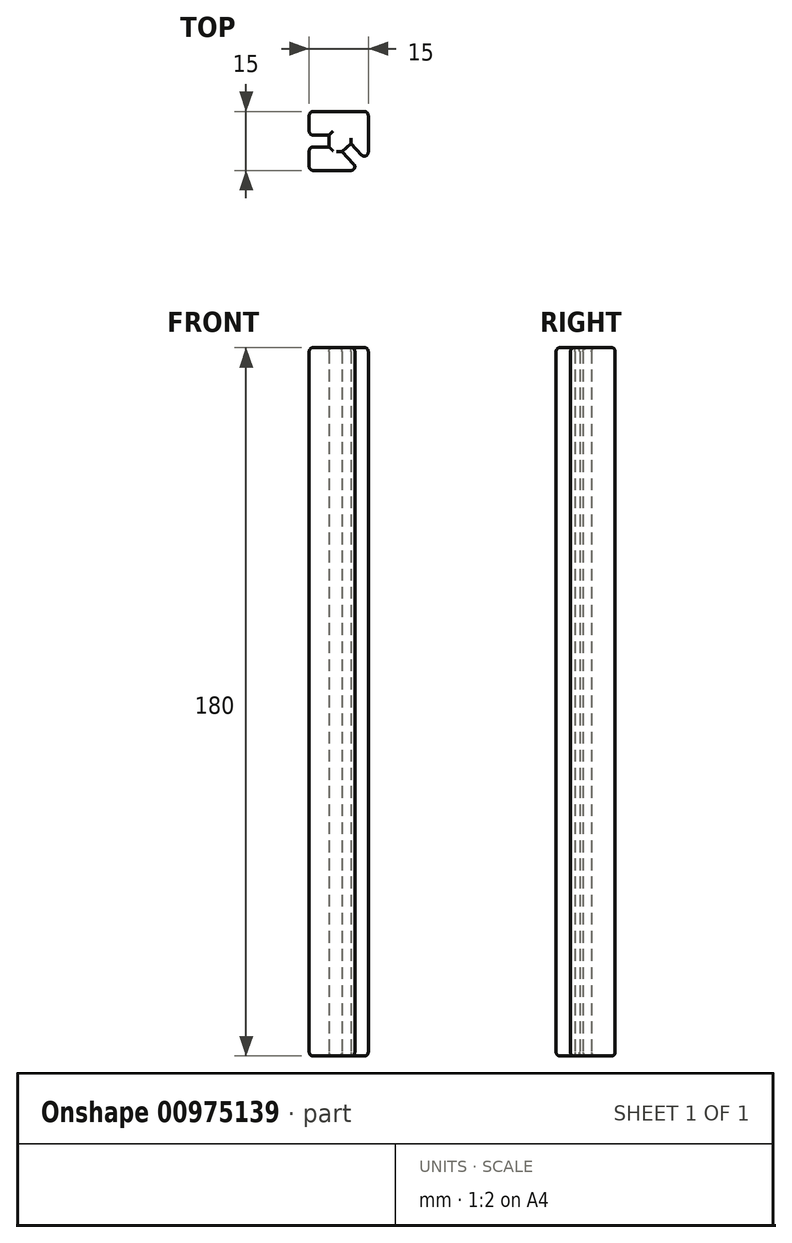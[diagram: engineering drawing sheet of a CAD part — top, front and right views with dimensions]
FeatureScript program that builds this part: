
annotation { "Feature Type Name" : "Feature", "Feature Type Description" : "" }
export const myFeature = defineFeature(function(context is Context, id is Id, definition is map)
    precondition{}
    {
        {
            var Q0;
            Q0=qCreatedBy(makeId("Top.planeOp"),FACE);
            var sketch = newSketch(context, id + "F0", { "sketchPlane" : qUnion([Q0])});
            skLineSegment(sketch, "E0.bottom", {"start": v(-7.5, 7.5) * mm, "end": v(7.5, 7.5) * mm});
            skLineSegment(sketch, "E0.top", {"start": v(-7.5, -7.5) * mm, "end": v(5.43, -7.5) * mm});
            skLineSegment(sketch, "E0.left", {"start": v(-7.5, 7.5) * mm, "end": v(-7.5, 1.5) * mm});
            skLineSegment(sketch, "E0.right", {"start": v(7.5, 7.5) * mm, "end": v(7.5, -5.33) * mm});
            skLineSegment(sketch, "E1.bottom", {"start": v(-7.5, 1.5) * mm, "end": v(-2.5, 1.5) * mm});
            skLineSegment(sketch, "E1.top", {"start": v(-7.5, -1.5) * mm, "end": v(-2.5, -1.5) * mm});
            skLineSegment(sketch, "E1.right", {"start": v(-2.5, 1.5) * mm, "end": v(-2.5, -1.5) * mm});
            skLineSegment(sketch, "E2.trimOffspring", {"start": v(-7.5, -1.5) * mm, "end": v(-7.5, -7.5) * mm});
            skLineSegment(sketch, "E3.0", {"start": v(0.89, -2.75) * mm, "end": v(5.43, -7.5) * mm});
            skLineSegment(sketch, "E4.0", {"start": v(3.06, -0.68) * mm, "end": v(7.5, -5.33) * mm});
            skLineSegment(sketch, "E5", {"start": v(3.06, -0.68) * mm, "end": v(0.89, -2.75) * mm});
            skPoint(sketch, "E6.orphan", {"position": v(7.5, -7.5) * mm});
            skSolve(sketch);
        }
        {
            var Q0;
            Q0=makeQuery(id+"F0.imprint","IMPRINT",FACE,{"disambiguationData":[TD([[makeQuery(id+"F0.imprint","IMPRINT",EDGE,{"derivedFrom":sQuery(id+"F0.wireOp",EDGE,"E0.bottom")}),-1.0]])]});
            extrude(context, id + "F1", {"entities" : qUnion([Q0]), "depth" : 180 * mm, "offsetDistance" : 25 * mm});
        }
        {
            var Q0;
            Q0=makeQuery(id+"F1.opExtrude","CAP_EDGE",EDGE,{"disambiguationData":[OSD([sQuery(id+"F0.wireOp",EDGE,"E1.top")])],"isStart":false});
            var Q1;
            Q1=makeQuery(id+"F1.opExtrude","CAP_EDGE",EDGE,{"disambiguationData":[OSD([sQuery(id+"F0.wireOp",EDGE,"E1.right")])],"isStart":false});
            var Q2;
            Q2=makeQuery(id+"F1.opExtrude","CAP_EDGE",EDGE,{"disambiguationData":[OSD([sQuery(id+"F0.wireOp",EDGE,"E1.bottom")])],"isStart":false});
            var Q3;
            Q3=makeQuery(id+"F1.opExtrude","CAP_EDGE",EDGE,{"disambiguationData":[OSD([sQuery(id+"F0.wireOp",EDGE,"E4.0")])],"isStart":false});
            var Q4;
            Q4=makeQuery(id+"F1.opExtrude","CAP_EDGE",EDGE,{"disambiguationData":[OSD([sQuery(id+"F0.wireOp",EDGE,"E5")])],"isStart":false});
            var Q5;
            Q5=makeQuery(id+"F1.opExtrude","CAP_EDGE",EDGE,{"disambiguationData":[OSD([sQuery(id+"F0.wireOp",EDGE,"E3.0")])],"isStart":false});
            var Q6;
            Q6=makeQuery(id+"F1.opExtrude","CAP_EDGE",EDGE,{"disambiguationData":[OSD([sQuery(id+"F0.wireOp",EDGE,"E0.top")])],"isStart":false});
            var Q7;
            Q7=makeQuery(id+"F1.opExtrude","CAP_EDGE",EDGE,{"disambiguationData":[OSD([sQuery(id+"F0.wireOp",EDGE,"E2.trimOffspring")])],"isStart":false});
            var Q8;
            Q8=makeQuery(id+"F1.opExtrude","CAP_EDGE",EDGE,{"disambiguationData":[OSD([sQuery(id+"F0.wireOp",EDGE,"E0.left")])],"isStart":false});
            var Q9;
            Q9=makeQuery(id+"F1.opExtrude","CAP_EDGE",EDGE,{"disambiguationData":[OSD([sQuery(id+"F0.wireOp",EDGE,"E0.bottom")])],"isStart":false});
            var Q10;
            Q10=makeQuery(id+"F1.opExtrude","CAP_EDGE",EDGE,{"disambiguationData":[OSD([sQuery(id+"F0.wireOp",EDGE,"E0.right")])],"isStart":false});
            var Q11;
            Q11=makeQuery(id+"F1.opExtrude","SWEPT_EDGE",EDGE,{"disambiguationData":[OSD([sQuery(id+"F0.wireOp",EDGE,"E0.top"),sQuery(id+"F0.wireOp",EDGE,"E2.trimOffspring")])]});
            var Q12;
            Q12=makeQuery(id+"F1.opExtrude","SWEPT_EDGE",EDGE,{"disambiguationData":[OSD([sQuery(id+"F0.wireOp",EDGE,"E1.top"),sQuery(id+"F0.wireOp",EDGE,"E2.trimOffspring")])]});
            var Q13;
            Q13=makeQuery(id+"F1.opExtrude","SWEPT_EDGE",EDGE,{"disambiguationData":[OSD([sQuery(id+"F0.wireOp",EDGE,"E0.left"),sQuery(id+"F0.wireOp",EDGE,"E1.bottom")])]});
            var Q14;
            Q14=makeQuery(id+"F1.opExtrude","SWEPT_EDGE",EDGE,{"disambiguationData":[OSD([sQuery(id+"F0.wireOp",EDGE,"E0.bottom"),sQuery(id+"F0.wireOp",EDGE,"E0.left")])]});
            var Q15;
            Q15=makeQuery(id+"F1.opExtrude","SWEPT_EDGE",EDGE,{"disambiguationData":[OSD([sQuery(id+"F0.wireOp",EDGE,"E0.top"),sQuery(id+"F0.wireOp",EDGE,"E3.0")])]});
            var Q16;
            Q16=makeQuery(id+"F1.opExtrude","SWEPT_EDGE",EDGE,{"disambiguationData":[OSD([sQuery(id+"F0.wireOp",EDGE,"E0.right"),sQuery(id+"F0.wireOp",EDGE,"E4.0")])]});
            var Q17;
            Q17=makeQuery(id+"F1.opExtrude","SWEPT_EDGE",EDGE,{"disambiguationData":[OSD([sQuery(id+"F0.wireOp",EDGE,"E0.bottom"),sQuery(id+"F0.wireOp",EDGE,"E0.right")])]});
            var Q18;
            Q18=makeQuery(id+"F1.opExtrude","CAP_FACE",FACE,{"disambiguationData":[OSD([sQuery(id+"F0.wireOp",EDGE,"E0.bottom"),sQuery(id+"F0.wireOp",EDGE,"E0.top"),sQuery(id+"F0.wireOp",EDGE,"E0.left"),sQuery(id+"F0.wireOp",EDGE,"E0.right"),sQuery(id+"F0.wireOp",EDGE,"E1.bottom"),sQuery(id+"F0.wireOp",EDGE,"E1.top"),sQuery(id+"F0.wireOp",EDGE,"E1.right"),sQuery(id+"F0.wireOp",EDGE,"E2.trimOffspring"),sQuery(id+"F0.wireOp",EDGE,"E3.0"),sQuery(id+"F0.wireOp",EDGE,"E4.0"),sQuery(id+"F0.wireOp",EDGE,"E5")])],"isStart":true});
            fillet(context, id + "F2", {"entities" : qUnion([Q0, Q1, Q2, Q3, Q4, Q5, Q6, Q7, Q8, Q9, Q10, Q11, Q12, Q13, Q14, Q15, Q16, Q17, Q18]), "radius" : 1 * mm, "tangentPropagation" : true, "allowEdgeOverflow" : false});
        }
    });
